# Revit family: Table-Teknion-Zones_ZNTLT-R2015
name_source: partatom
category: Furniture
revit_build: Autodesk Revit 2015 (Build: 20140223_1515(x64)
units: mm (PartAtom-declared; Revit-internal decimal feet)

## types (3) — shared parameters
Assembly Code = E2020200
Depth = 11"
Manufacturer = Teknion
Manufacturer Fax = 416.661.4586
Part Number = ZNTLT
Product Documentation Link = http://www.teknion.com
Product Line = Zones
Product Page URL = http://www.teknion.com
Series = Zones
Sustainability Data = http://www.teknion.com
URL = http://www.teknion.com
Warranty = http://www.teknion.com

## per-type parameters (varying)
| type | Description | Height | Model | Pencil Edge | Width |
| Pencil Edge with Exposed Birch Ply | Laptop Table, Pencil Edge with  Exposed Birch Ply | 26 9/32" | ZNTLT261133B | Yes | 32 7/8" |
| Knife Edge | Laptop Table, Knife Edge | 26" | ZNTLT261133C | No | 33" |
| Pencil Edge with Solid Beech | Laptop Table, Pencil Edge with  Solid Beech | 26 9/32" | ZNTLT261133D | Yes | 32 7/8" |

type visibility flags (boolean, named after types; folded from table):
- Pencil Edge with Exposed Birch Ply: Yes: (none)
- Knife Edge: Yes: Knife Edge
- Pencil Edge with Solid Beech: Yes: (none)

## geometry (parser evidence)
native form markers: Blend x58, Sweep x2
no freeform markers — native parametric forms only
